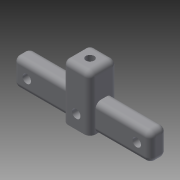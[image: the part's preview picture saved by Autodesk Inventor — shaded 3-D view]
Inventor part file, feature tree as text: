
AUTODESK INVENTOR PART (.ipt)
format: ipt  version: 2015 (Build 190159000, 159)  size: 190,976 bytes
history: native  units: mm
features: sketch x5, hole x3, fillet x3, extrude x2, plane x2, mirror x1
ambient origin geometry x8: Origin, YZ Plane, XZ Plane, XY Plane, X Axis, Y Axis, Z Axis, Center Point
bodies: Body1 (feature_tree)
feature tree (16):
  extrude  "Extrusion3"  Depth=10.0mm
  hole  "Hole4"  [1 undecoded]
  hole  "Hole5"  [1 undecoded]
  extrude  "Extrusion4"  Depth=6.0mm
  plane  "Work Plane2"
  hole  "Hole6"  [1 undecoded]
  plane  "Work Plane1"
  mirror  "Mirror1"
  fillet  "Fillet3"  Radius=5.0mm
  fillet  "Fillet4"  Radius=2.0mm
  fillet  "Fillet5"  Radius=2.0mm
  sketch  "Sketch6"  dims[d31=10.0mm d32=10.0mm]
  sketch  "Sketch7"  dims[d33=5.0mm d34=5.0mm]
  sketch  "Sketch8"  dims[d35=20.0mm d36=0.0mm]
  sketch  "Sketch9"  dims[d37=3.0mm d38=6.0mm d39=4.0mm d40=2.0mm d41=90.0deg d42=8.0mm d43=0.0mm d44=5.0mm]
  sketch  "Sketch10"  dims[d45=3.1mm d46=6.0mm d47=4.0mm d48=5.0mm d49=90.0deg d50=8.0mm d51=0.0mm d52=6.0mm d53=20.0mm d54=0.0mm d56=5.0mm d57=3.1mm d58=6.0mm d59=4.0mm d60=3.0mm d61=90.0deg d62=8.0mm d63=0.0mm d64=2.0mm d65=2.0mm d66=2.0mm]
note: 3 required parameter values undecoded (feature->parameter linkage not recoverable at this tier; creation-order binding heuristic only, values carry confidence <= 0.55)
